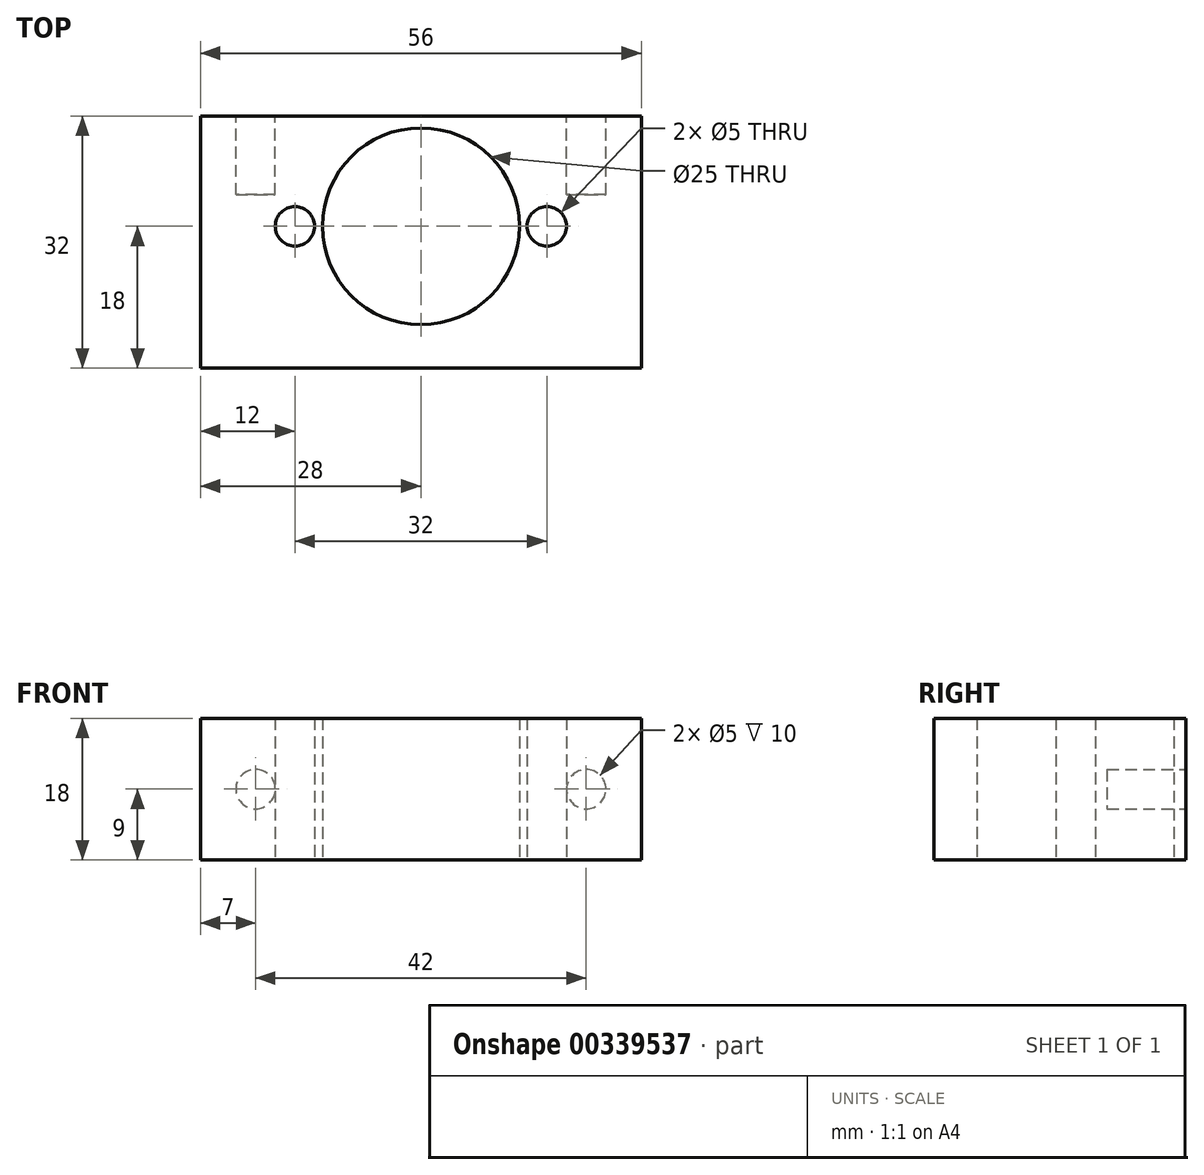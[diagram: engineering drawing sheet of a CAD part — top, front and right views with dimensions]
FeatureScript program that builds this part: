
annotation { "Feature Type Name" : "Feature", "Feature Type Description" : "" }
export const myFeature = defineFeature(function(context is Context, id is Id, definition is map)
    precondition{}
    {
        {
            var Q0;
            Q0=qCreatedBy(makeId("Top.planeOp"),FACE);
            var sketch = newSketch(context, id + "F0", { "sketchPlane" : qUnion([Q0])});
            skLineSegment(sketch, "E0.bottom", {"start": v(-28, 0) * mm, "end": v(28, 0) * mm});
            skLineSegment(sketch, "E0.top", {"start": v(-28, -32) * mm, "end": v(28, -32) * mm});
            skLineSegment(sketch, "E0.left", {"start": v(-28, 0) * mm, "end": v(-28, -32) * mm});
            skLineSegment(sketch, "E0.right", {"start": v(28, 0) * mm, "end": v(28, -32) * mm});
            skLineSegment(sketch, "E1", {"start": v(-28, -14) * mm, "end": v(28, -14) * mm, "construction": true});
            skLineSegment(sketch, "E2", {"start": v(0, 0) * mm, "end": v(0, -32) * mm, "construction": true});
            skCircle(sketch, "E3", {"center": v(0, -14) * mm, "radius": 12.5 * mm});
            skCircle(sketch, "E4", {"center": v(0, -14) * mm, "radius": 16 * mm, "construction": true});
            skCircle(sketch, "E5", {"center": v(-16, -14) * mm, "radius": 2.5 * mm});
            skCircle(sketch, "E6", {"center": v(16, -14) * mm, "radius": 2.5 * mm});
            skCircle(sketch, "E7", {"center": v(0, -14) * mm, "radius": 21 * mm, "construction": true});
            skSolve(sketch);
        }
        {
            var Q0;
            Q0=makeQuery(id+"F0.imprint","IMPRINT",FACE,{"disambiguationData":[TD([[makeQuery(id+"F0.imprint","IMPRINT",EDGE,{"derivedFrom":sQuery(id+"F0.wireOp",EDGE,"E0.bottom")}),-1.0]])]});
            extrude(context, id + "F1", {"entities" : qUnion([Q0]), "depth" : 18 * mm});
        }
        {
            var Q0;
            Q0=makeQuery(id+"F1.opExtrude","SWEPT_FACE",FACE,{"disambiguationData":[OSD([sQuery(id+"F0.wireOp",EDGE,"E0.bottom")])]});
            var sketch = newSketch(context, id + "F2", { "sketchPlane" : qUnion([Q0])});
            skLineSegment(sketch, "E8", {"start": v(28, 9) * mm, "end": v(-28, 9) * mm});
            skCircle(sketch, "E9", {"center": v(21, 9) * mm, "radius": 2.5 * mm});
            skCircle(sketch, "E10", {"center": v(-21, 9) * mm, "radius": 2.5 * mm});
            skSolve(sketch);
        }
        {
            var Q0;
            Q0 = qSketchRegion(id + "F2", true);
            extrude(context, id + "F3", {"entities" : qUnion([Q0]), "operationType" : NewBodyOperationType.REMOVE, "oppositeDirection" : true, "depth" : 10 * mm});
        }
    });
